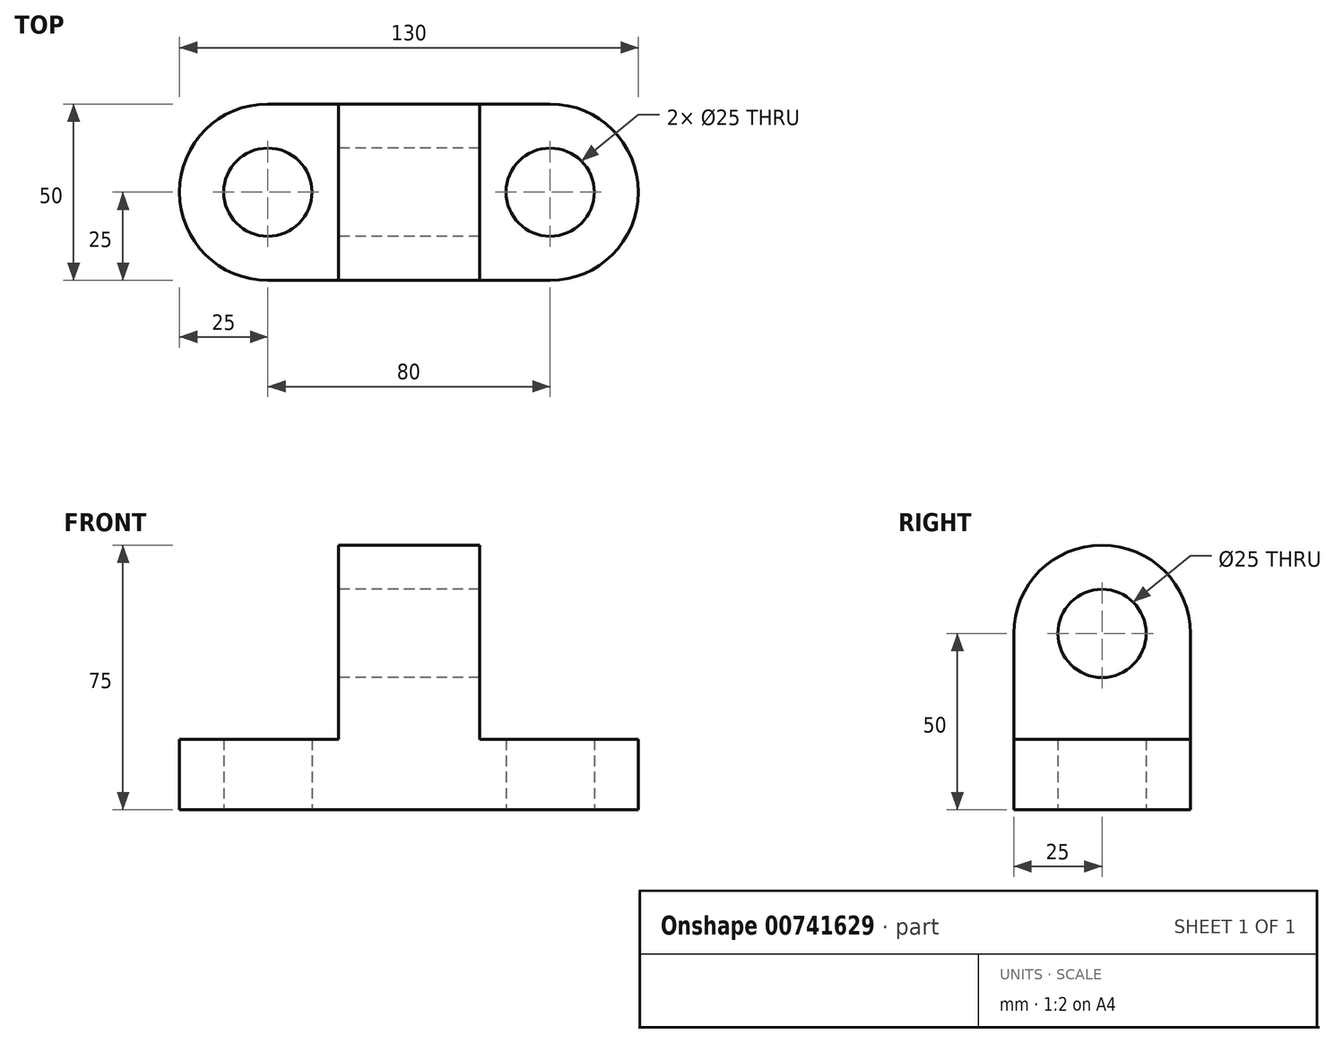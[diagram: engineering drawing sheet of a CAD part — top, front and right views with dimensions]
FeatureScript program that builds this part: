
annotation { "Feature Type Name" : "Feature", "Feature Type Description" : "" }
export const myFeature = defineFeature(function(context is Context, id is Id, definition is map)
    precondition{}
    {
        {
            var Q0;
            Q0=qCreatedBy(makeId("Front.planeOp"),FACE);
            var sketch = newSketch(context, id + "F0", { "sketchPlane" : qUnion([Q0])});
            skLineSegment(sketch, "E0", {"start": v(0, 0) * mm, "end": v(80, 0) * mm});
            skLineSegment(sketch, "E1", {"start": v(80, 0) * mm, "end": v(80, 19.39) * mm});
            skLineSegment(sketch, "E2", {"start": v(80, 19.39) * mm, "end": v(60, 19.39) * mm});
            skLineSegment(sketch, "E3", {"start": v(60, 19.39) * mm, "end": v(60, 50) * mm});
            skLineSegment(sketch, "E4", {"start": v(60, 50) * mm, "end": v(20, 50) * mm});
            skLineSegment(sketch, "E5", {"start": v(20, 50) * mm, "end": v(20, 20) * mm});
            skLineSegment(sketch, "E6", {"start": v(20, 20) * mm, "end": v(0, 20) * mm});
            skLineSegment(sketch, "E7", {"start": v(0, 20) * mm, "end": v(0, 0) * mm});
            skSolve(sketch);
        }
        {
            var Q0;
            Q0=qCreatedBy(makeId("Top.planeOp"),FACE);
            var sketch = newSketch(context, id + "F1", { "sketchPlane" : qUnion([Q0])});
            skLineSegment(sketch, "E8", {"start": v(0, 0) * mm, "end": v(80, 0) * mm});
            skLineSegment(sketch, "E9", {"start": v(80, -50) * mm, "end": v(0, -50) * mm});
            skArc(sketch, "E10", {"start": v(80, -50) * mm, "mid": v(105, -25) * mm, "end": v(80, 0) * mm});
            skArc(sketch, "E11", {"start": v(0, 0) * mm, "mid": v(-25, -25) * mm, "end": v(0, -50) * mm});
            skCircle(sketch, "E12", {"center": v(0, -25) * mm, "radius": 12.5 * mm});
            skCircle(sketch, "E13", {"center": v(80, -25) * mm, "radius": 12.5 * mm});
            skSolve(sketch);
        }
        {
            var Q0;
            Q0 = qSketchRegion(id + "F1", true);
            extrude(context, id + "F2", {"entities" : qUnion([Q0]), "depth" : 20 * mm, "offsetDistance" : 25 * mm});
        }
        {
            var Q0;
            Q0 = qSketchRegion(id + "F0", true);
            extrude(context, id + "F3", {"entities" : qUnion([Q0]), "operationType" : NewBodyOperationType.ADD, "depth" : 50 * mm, "offsetDistance" : 25 * mm});
        }
        {
            var Q0;
            Q0=makeQuery(id+"F1.imprint","IMPRINT",FACE,{"disambiguationData":[TD([[makeQuery(id+"F1.imprint","IMPRINT",EDGE,{"derivedFrom":sQuery(id+"F1.wireOp",EDGE,"E12")}),1.0]])]});
            var Q1;
            Q1=makeQuery(id+"F1.imprint","IMPRINT",FACE,{"disambiguationData":[TD([[makeQuery(id+"F1.imprint","IMPRINT",EDGE,{"derivedFrom":sQuery(id+"F1.wireOp",EDGE,"E13")}),1.0]])]});
            var Q2;
            Q2=sQuery(id+"F1.wireOp",EDGE,"E12");
            var Q3;
            Q3=sQuery(id+"F1.wireOp",EDGE,"E13");
            extrude(context, id + "F4", {"entities" : qUnion([Q0, Q1]), "operationType" : NewBodyOperationType.REMOVE, "surfaceEntities" : qUnion([Q2, Q3]), "depth" : 25 * mm, "offsetDistance" : 25 * mm});
        }
        {
            var Q0;
            Q0=makeQuery(id+"F3.opExtrude","SWEPT_FACE",FACE,{"disambiguationData":[OSD([sQuery(id+"F0.wireOp",EDGE,"E5")])]});
            var sketch = newSketch(context, id + "F5", { "sketchPlane" : qUnion([Q0])});
            skLineSegment(sketch, "E14", {"start": v(0, 50) * mm, "end": v(50, 50) * mm});
            skArc(sketch, "E15", {"start": v(50, 50) * mm, "mid": v(25, 75) * mm, "end": v(0, 50) * mm});
            skCircle(sketch, "E16", {"center": v(25, 50) * mm, "radius": 12.5 * mm});
            skSolve(sketch);
        }
        {
            var Q0;
            {var subQ0=sQuery(id+"F5.wireOp",EDGE,"E15");Q0=makeQuery(id+"F5.imprint","IMPRINT",FACE,{"disambiguationData":[TD([[makeQuery(id+"F5.imprint","IMPRINT",EDGE,{"derivedFrom":subQ0}),1.0]])]});}
            extrude(context, id + "F6", {"entities" : qUnion([Q0]), "operationType" : NewBodyOperationType.ADD, "oppositeDirection" : true, "depth" : 40 * mm, "offsetDistance" : 25 * mm});
        }
        {
            var Q0;
            {var subQ0=sQuery(id+"F5.wireOp",EDGE,"E16");var subQ1=sQuery(id+"F5.wireOp",EDGE,"E14");var subQ2=makeQuery(id+"F5.imprint","INTERSECT",VERTEX,{"disambiguationData":[OD(0.0)],"derivedFrom":[subQ1,subQ0]});Q0=makeQuery(id+"F5.imprint","IMPRINT",FACE,{"disambiguationData":[TD([[makeQuery(id+"F5.imprint","IMPRINT",EDGE,{"disambiguationData":[TD([[subQ2,-1.0]])],"derivedFrom":subQ1}),1.0]])]});}
            extrude(context, id + "F7", {"entities" : qUnion([Q0]), "operationType" : NewBodyOperationType.REMOVE, "oppositeDirection" : true, "depth" : 40 * mm, "offsetDistance" : 25 * mm});
        }
    });
